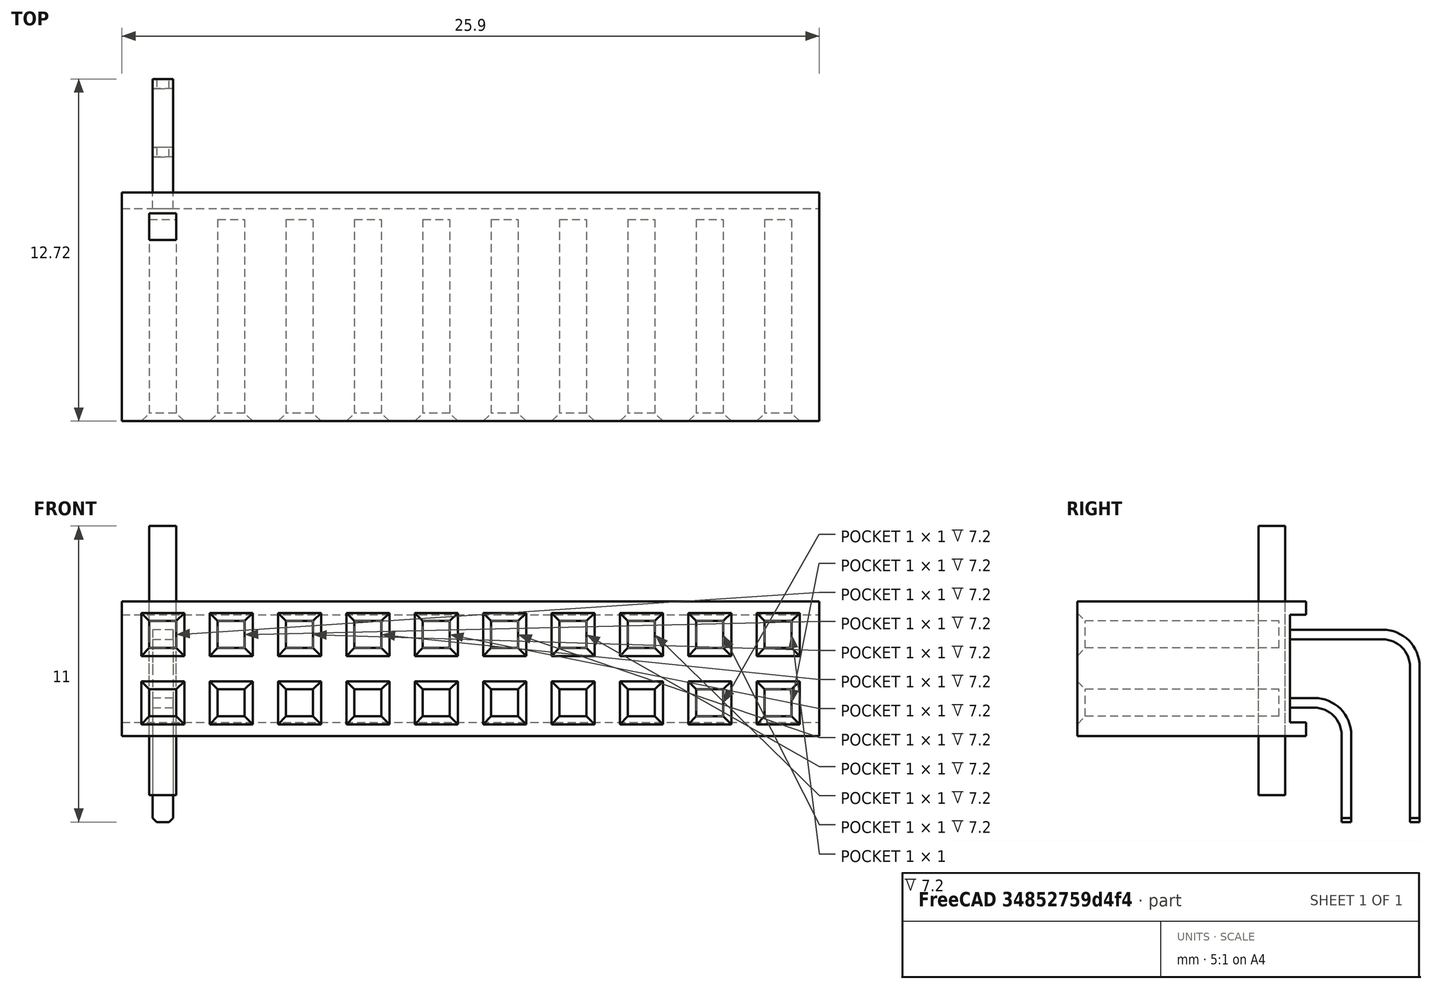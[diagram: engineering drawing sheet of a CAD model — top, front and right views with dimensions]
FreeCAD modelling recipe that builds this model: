
FCSTD DOCUMENT  (FreeCAD 0.19R24291 (Git))
Label: A2541HWR-2x10P
License: All rights reserved
LicenseURL: http://en.wikipedia.org/wiki/All_rights_reserved
objects: Part::Box×3, Part::FeaturePython×3, Part::Chamfer×3, Part::Cut×2, Part::Sweep×2
note: 10 computed .brp shape members not serialized (recipe doc carries the construction recipe); baked Part::Feature solids carry a one-line shape summary decoded from their .brp

FEATURE [Part::Box] Box  label="Cube"
  AttacherType = Attacher::AttachEngine3D
  Height = 8.5
  Length = 25.9
  Placement = pos=(-12.95,-2.5,0) rot=(0,0,1;0rad)
  Width = 5
  expr: .Placement.Base.y = -(Width / 2)
  expr: .Placement.Base.x = -(Length / 2)
  expr: Length = 2.54 * 10 + 0.5
FEATURE [Part::Box] Box001  label="Cube001"
  AttacherType = Attacher::AttachEngine3D
  Height = 10
  Length = 1
  Placement = pos=(-11.93,-1.77,1) rot=(0,0,1;0rad)
  Width = 1
  expr: .Placement.Base.x = -(2.54 * 4 + 1.27 + 0.5)
FEATURE [Part::FeaturePython] Array  # Draft array (typed FeaturePython)
  Angle = 360
  ArrayType = 0
  Axis = (0,0,1)
  Base = -> Box001
  Center = (0,0,0)
  Count = 20
  ExpandArray = false
  Fuse = false
  IntervalAxis = (0,0,0)
  IntervalX = (2.54,0,0)
  IntervalY = (0,2.54,0)
  IntervalZ = (0,0,100)
  NumberCircles = 3
  NumberPolar = 5
  NumberX = 10
  NumberY = 2
  NumberZ = 1
  PlacementList = 20 placements: [(-11.93,-1.77,1),(-11.93,0.77,1),(-9.39,-1.77,1),(-9.39,0.77,1),(-6.85,-1.77,1),(-6.85,0.77,1),(-4.31,-1.77,1),(-4.31,0.77,1),(-1.77,-1.77,1),(-1.77,0.77,1),(0.77,-1.77,1),(0.77,0.77,1),(3.31,-1.77,1),(3.31,0.77,1),(5.85,-1.77,1),(5.85,0.77,1),(8.39,-1.77,1),(8.39,0.77,1),(10.93,-1.77,1),(10.93,0.77,1)]
  RadialDistance = 50
  ScaleList = (20) [(1,1,1),(1,1,1),(1,1,1),(1,1,1),(1,1,1),(1,1,1),(1,1,1),(1,1,1),(1,1,1),(1,1,1),(1,1,1),(1,1,1),(1,1,1),(1,1,1),(1,1,1),(1,1,1),(1,1,1),(1,1,1),(1,1,1),(1,1,1)]
  Symmetry = 1
  TangentialDistance = 25
FEATURE [Part::Cut] Cut
  Base = -> Box
  Tool = -> Array
FEATURE [Part::Box] Box002  label="Cube002"
  AttacherType = Attacher::AttachEngine3D
  Height = 0.6
  Length = 26
  Placement = pos=(-13,-2,0) rot=(0,0,1;0rad)
  Width = 4
FEATURE [Part::Cut] Cut001
  Base = -> Cut
  Tool = -> Box002
FEATURE [Part::Chamfer] Chamfer
  Base = -> Cut001
  Edges = 80 edges r=0.3: [Edge12,Edge13,Edge14,Edge15,Edge16,Edge17,Edge18,Edge19,Edge20,Edge21,Edge22,Edge23,Edge24,Edge25,Edge26,Edge27,Edge28,Edge29,Edge30,Edge31,Edge32,Edge33,Edge34,Edge35,Edge36,Edge37,Edge38,Edge39,Edge40,Edge41,Edge42,Edge43,Edge44,Edge45,Edge46,Edge47,Edge48,Edge49,Edge50,Edge51,Edge52,Edge53,+38 more]
  Placement = pos=(0,0,5.7) rot=(1,0,0;1.5708rad)
FEATURE [Part::Sweep] Sweep
  Frenet = false
  Placement = pos=(-11.43,0,0) rot=(0,0,1;0rad)
  Solid = true
  Transition = 1
FEATURE [Part::Sweep] Sweep002
  Frenet = false
  Placement = pos=(-11.43,0,0) rot=(0,0,1;0rad)
  Solid = true
  Transition = 1
FEATURE [Part::Chamfer] Chamfer001
  Base = -> Sweep002
  Edges = 2 edges r=0.15: [Edge25,Edge28]
FEATURE [Part::Chamfer] Chamfer002
  Base = -> Sweep
  Edges = 2 edges r=0.15: [Edge25,Edge28]
FEATURE [Part::FeaturePython] Array001  # Draft array (typed FeaturePython)
  Angle = 360
  ArrayType = 0
  Axis = (0,0,1)
  Base = -> Chamfer001
  Center = (0,0,0)
  Count = 10
  ExpandArray = false
  Fuse = false
  IntervalAxis = (0,0,0)
  IntervalX = (2.54,0,0)
  IntervalY = (0,100,0)
  IntervalZ = (0,0,100)
  NumberCircles = 3
  NumberPolar = 5
  NumberX = 10
  NumberY = 1
  NumberZ = 1
  PlacementList = 10 placements: arithmetic series from (0,0,0) step (2.54,0,0) to (22.86,0,0)
  RadialDistance = 50
  ScaleList = (10) [(1,1,1),(1,1,1),(1,1,1),(1,1,1),(1,1,1),(1,1,1),(1,1,1),(1,1,1),(1,1,1),(1,1,1)]
  Symmetry = 1
  TangentialDistance = 25
FEATURE [Part::FeaturePython] Array002  # Draft array (typed FeaturePython)
  Angle = 360
  ArrayType = 0
  Axis = (0,0,1)
  Base = -> Chamfer002
  Center = (0,0,0)
  Count = 10
  ExpandArray = false
  Fuse = false
  IntervalAxis = (0,0,0)
  IntervalX = (2.54,0,0)
  IntervalY = (0,100,0)
  IntervalZ = (0,0,100)
  NumberCircles = 3
  NumberPolar = 5
  NumberX = 10
  NumberY = 1
  NumberZ = 1
  PlacementList = 10 placements: arithmetic series from (0,0,0) step (2.54,0,0) to (22.86,0,0)
  RadialDistance = 50
  ScaleList = (10) [(1,1,1),(1,1,1),(1,1,1),(1,1,1),(1,1,1),(1,1,1),(1,1,1),(1,1,1),(1,1,1),(1,1,1)]
  Symmetry = 1
  TangentialDistance = 25
